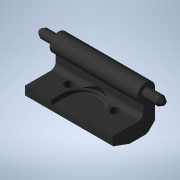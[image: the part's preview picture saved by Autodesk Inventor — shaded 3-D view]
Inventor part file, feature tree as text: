
AUTODESK INVENTOR PART (.ipt)
format: ipt  version: 2021 (Build 250183000, 183)  size: 196,096 bytes
history: native  units: mm
features: other x14, sketch x6, extrude x2, hole x2, revolve x2
ambient origin geometry x8: Origin, YZ Plane, XZ Plane, XY Plane, X Axis, Y Axis, Z Axis, Center Point
bodies: Solid1 (feature_tree)
feature tree (26):
  extrude  "Extrusion1"  Depth=3.7mm TaperAngle=0.0deg
  hole  "Hole1"  [1 undecoded]
  hole  "Hole2"  [1 undecoded]
  extrude  "Extrusion2"  [1 undecoded]
  revolve  "Revolution1"  [1 undecoded]
  revolve  "Revolution2"  [1 undecoded]
  other  "DECKEL_XY"
  other  "DECKEL_YZ"
  other  "DECKEL_ZX"
  other  "DECKEL_X"
  other  "DECKEL_Y"
  other  "DECKEL_Z"
  other  "DECKEL_Center"
  other  "HINGE_XY"
  other  "HINGE_YZ"
  other  "HINGE_ZX"
  other  "HINGE_X"
  other  "HINGE_Y"
  other  "HINGE_Z"
  other  "HINGE_Center"
  sketch  "Sketch_1"  dims[d0=24.8mm d1=0.0mm]
  sketch  "Sketch2"  dims[d2=2.459mm d3=6.0mm d4=4.0mm d5=2.0mm d6=90.0deg d7=5.75mm d8=0.0mm]
  sketch  "Sketch3"  dims[d9=2.459mm d10=6.0mm d11=4.0mm d12=2.0mm d13=90.0deg d14=5.75mm d15=0.0mm d16=3.7mm d17=0.0mm]
  sketch  "Sketch_5"  dims[d18=180.0deg d19=360.0deg]
  sketch  "Sketch_6"
  sketch  "Sketch_8"
note: 5 required parameter values undecoded (feature->parameter linkage not recoverable at this tier; creation-order binding heuristic only, values carry confidence <= 0.55)
